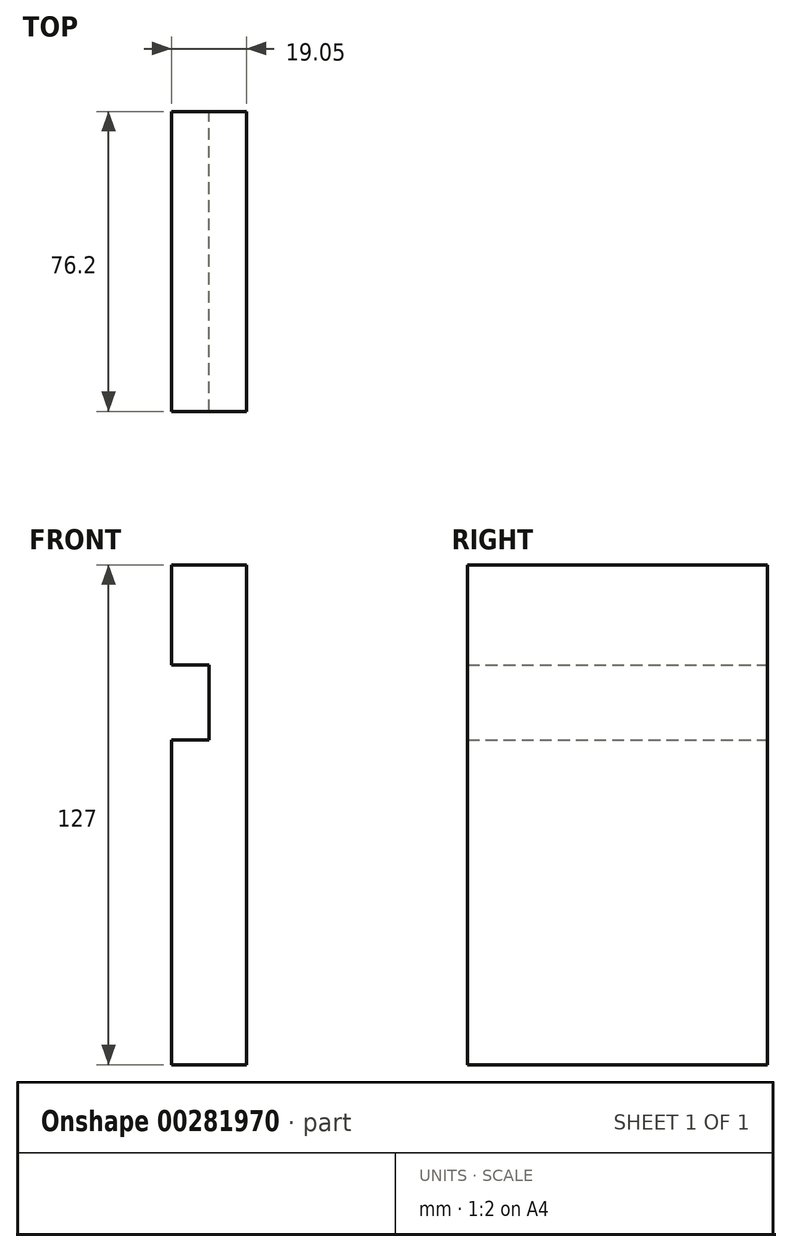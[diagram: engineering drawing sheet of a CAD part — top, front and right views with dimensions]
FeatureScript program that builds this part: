
annotation { "Feature Type Name" : "Feature", "Feature Type Description" : "" }
export const myFeature = defineFeature(function(context is Context, id is Id, definition is map)
    precondition{}
    {
        {
            var Q0;
            Q0=qCreatedBy(makeId("Front.planeOp"),FACE);
            var sketch = newSketch(context, id + "F0", { "sketchPlane" : qUnion([Q0])});
            skLineSegment(sketch, "E0", {"start": v(0, 0) * mm, "end": v(-19.05, 0) * mm});
            skLineSegment(sketch, "E1", {"start": v(0, 0) * mm, "end": v(0, 127) * mm});
            skLineSegment(sketch, "E2", {"start": v(-19.05, 0) * mm, "end": v(-19.05, 82.55) * mm});
            skLineSegment(sketch, "E3", {"start": v(-19.05, 82.55) * mm, "end": v(-9.53, 82.55) * mm});
            skLineSegment(sketch, "E4", {"start": v(-9.53, 82.55) * mm, "end": v(-9.53, 101.6) * mm});
            skLineSegment(sketch, "E5", {"start": v(-9.53, 101.6) * mm, "end": v(-19.05, 101.6) * mm});
            skLineSegment(sketch, "E6", {"start": v(-19.05, 101.6) * mm, "end": v(-19.05, 127) * mm});
            skLineSegment(sketch, "E7", {"start": v(-19.05, 127) * mm, "end": v(0, 127) * mm});
            skSolve(sketch);
        }
        {
            var Q0;
            Q0 = qSketchRegion(id + "F0", true);
            extrude(context, id + "F1", {"entities" : qUnion([Q0]), "depth" : 76.2 * mm});
        }
    });
